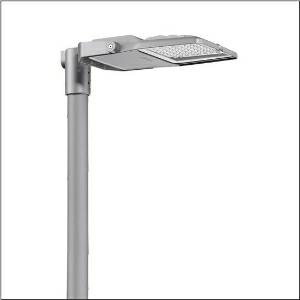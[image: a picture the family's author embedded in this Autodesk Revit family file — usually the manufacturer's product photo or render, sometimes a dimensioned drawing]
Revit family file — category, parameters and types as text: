
# Revit family: floodlight_fl_21_iq_mini___pl33t_5xa7772b4f3a_8cfb
name_source: partatom
category: Lighting Fixtures
units: mm (PartAtom-declared; Revit-internal decimal feet)

## family parameters
Cut with Voids When Loaded = No
Host = Face
Light Source = No
Part Type = Normal
Room Calculation Point = No
Round Connector Dimension = Use Diameter
Shared = No

## types (1)
- --- (1 x LED, 6420 lm, 45.5 W, 4000K)
    Apparent Load = 46 VA
    CIE Flux Codes = 26 75 99 100 100
    Color Rendering = 70
    Color Temperature = 4000K
    Default Elevation = 1800 mm
    Description = Floodlight FL 21 iQ mini, floodlight, primary light control with lens, of PMMA, primary optical cover: protective disc, of toughened safety glass, transparent, light distribution: PL33T, light emission: direct distribution, installation type: surface-mounted, LED, High Power LED, rated luminous flux: 6.420lm, luminous efficacy: 141lm/W, light colour: 740, colour temperature: 4000K, control gear: iQ Street-Remote/DALI, control: Auto-Match, Temp-Guard, Night-Set, Smart-Wire, Desk-Remote (wireless, voltage-free reading and setting of iQ features in the workshop via application-optimized NFC function/RFID function), optimised constant luminous flux control (CLO 2.0), Light-Fading, Lumen-Switch, with terminal, 6-pole, mains connection: 220..240V, AC, 50/60Hz, start of lifetime: 46W, end of service life: 48W, reduction: 22W, luminaire housing, of diecast aluminium, powder-coated, Siteco® metallic grey (DB 702S), corrosivity category C5 mid according to DIN EN ISO 12944, suitable for swimming pools, chlorine-resistant, sealing non-destructively replaceable, please order mast flange separately, mast bracket, of steel, galvanised, powder-coated, protection rating (complete): IP66, insulation class (complete): insulation class II (safety insulation), certification: CE, ENEC, VDE, protection symbol: D, impact resistance: IK08, permissible operating ambient temperature: -40..+40°C, permissible operating ambient temperature for outdoor applications: -40..+50°C, standard: DIN EN 12944, LABS conformity tested according to VDMA 24364:2018-05, packaging unit: 1 piece

Light Distribution: PL33T
    Height = 70 mm
    Lamp = 1 x LED
    Lamp Light Flux = 6420 lm
    Lamp Power = 45.5 W
    Lamp count = 1
    Length = 485 mm
    Luminous efficacy = 141 lm/W
    Manufacturer = Siteco
    ModVariant = No
    Model = 5XA7772B4F3A
    Number of Poles = 1
    OnlyDefault = Yes
    Power Factor = 1
    Product Name = Floodlight FL 21 iQ mini | PL33T
    Product group = floodlight | pylon annexe
    ProductGroupID = 6201
    Protection Class = Protection class II
    Protection Degree = IP 66
    RLX_Detail_Level = 1
    RLX_Emergency_Light_Flux = 0 lm
    RLX_Emergency_Type = 0
    RLX_Emergency_Type_DB = No
    RlxData = <blob elided: 101181 chars, md5=7a7074fa>
    Socket = socket
    Standby Power = 0 W
    System Light Flux = 6420 lm
    System Power = 46 W
    Type Comments = factory setting: luminous flux: 100 % | dim-lin: 254 | 463 mA
    Type Image = l_1007125.jpg
    URL = http://relux.com
    VarID = @adj_171329
    Voltage = 0 V
    Weight = 0.00 kg
    Width = 337 mm

## geometry (parser evidence)
native form markers: Blend x4, Sweep x12
no freeform markers — native parametric forms only
